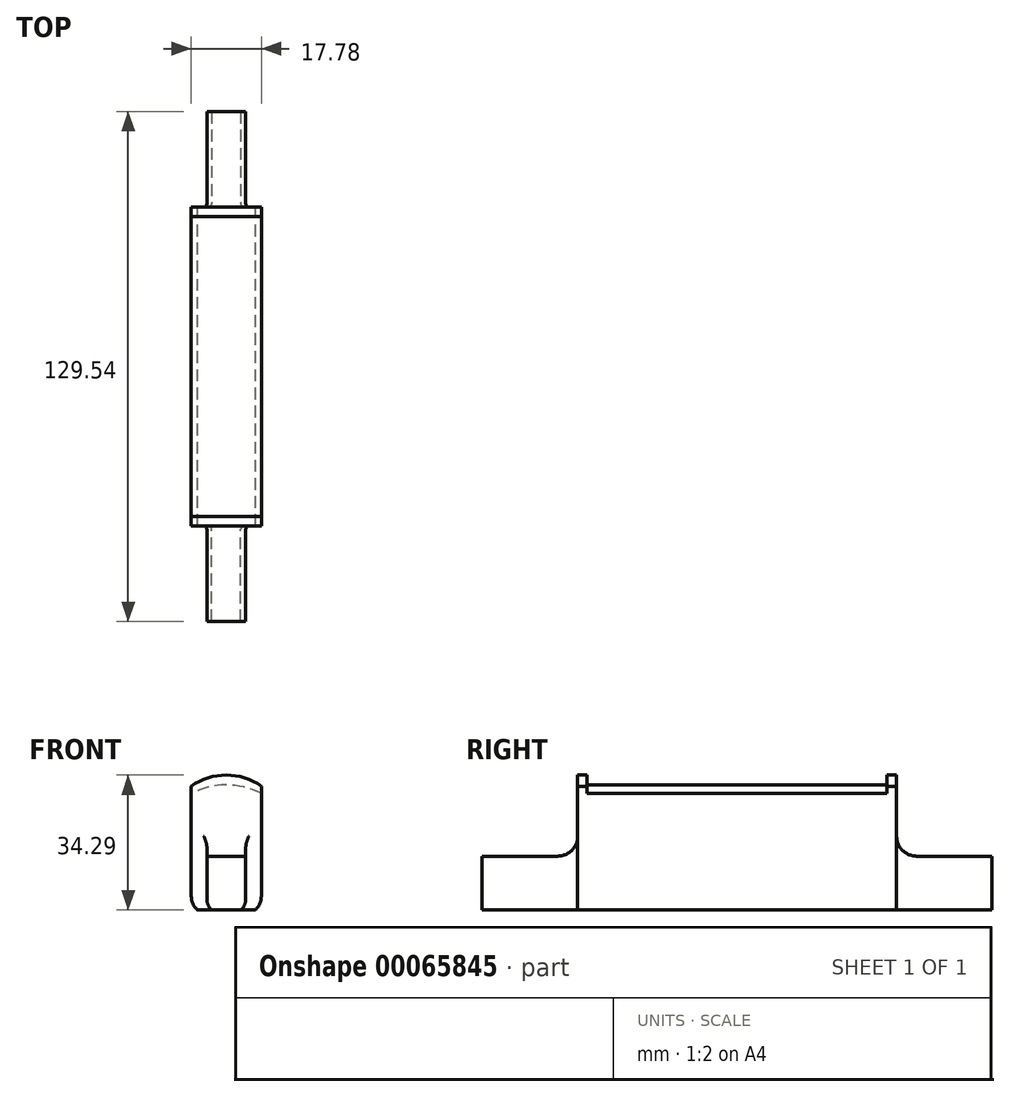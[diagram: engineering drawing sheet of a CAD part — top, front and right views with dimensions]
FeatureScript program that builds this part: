
annotation { "Feature Type Name" : "Feature", "Feature Type Description" : "" }
export const myFeature = defineFeature(function(context is Context, id is Id, definition is map)
    precondition{}
    {
        {
            var Q0;
            Q0=qCreatedBy(makeId("Front.planeOp"),FACE);
            var sketch = newSketch(context, id + "F0", { "sketchPlane" : qUnion([Q0])});
            skLineSegment(sketch, "E0.rect.bottom", {"start": v(8.9, 24.58) * mm, "end": v(-8.9, 24.58) * mm});
            skLineSegment(sketch, "E0.rect.top", {"start": v(8.89, -6.83) * mm, "end": v(-8.9, -6.83) * mm});
            skLineSegment(sketch, "E0.rect.left", {"start": v(8.89, 24.58) * mm, "end": v(8.89, -6.83) * mm});
            skLineSegment(sketch, "E0.rect.right", {"start": v(-8.9, 24.58) * mm, "end": v(-8.9, -6.83) * mm});
            skPoint(sketch, "E0.rect.middle", {"position": v(0, 8.87) * mm});
            skCircle(sketch, "E1", {"center": v(0, 0) * mm, "radius": 4.95 * mm});
            skArc(sketch, "E2", {"start": v(8.89, 24.58) * mm, "mid": v(0, 27.46) * mm, "end": v(-8.9, 24.58) * mm});
            skLineSegment(sketch, "E3.rect.bottom", {"start": v(-4.95, 6.83) * mm, "end": v(4.95, 6.83) * mm});
            skLineSegment(sketch, "E3.rect.top", {"start": v(-4.95, -6.83) * mm, "end": v(4.95, -6.83) * mm});
            skLineSegment(sketch, "E3.rect.left", {"start": v(-4.95, 6.83) * mm, "end": v(-4.95, -6.83) * mm});
            skLineSegment(sketch, "E3.rect.right", {"start": v(4.95, 6.83) * mm, "end": v(4.95, -6.83) * mm});
            skLineSegment(sketch, "E4", {"start": v(-8.89, 22.73) * mm, "end": v(8.9, 22.73) * mm});
            skArc(sketch, "E5", {"start": v(8.89, 22.73) * mm, "mid": v(0, 24.92) * mm, "end": v(-8.9, 22.73) * mm});
            skLineSegment(sketch, "E6", {"start": v(0, 27.46) * mm, "end": v(0, 24.92) * mm, "construction": true});
            skArc(sketch, "E7", {"start": v(-8.89, -3.43) * mm, "mid": v(-8.5, -5.3) * mm, "end": v(-7.37, -6.83) * mm});
            skArc(sketch, "E8", {"start": v(7.37, -6.83) * mm, "mid": v(8.5, -5.3) * mm, "end": v(8.9, -3.43) * mm});
            skArc(sketch, "E9", {"start": v(-4.95, -4.1) * mm, "mid": v(-4.62, -5.61) * mm, "end": v(-3.68, -6.83) * mm});
            skArc(sketch, "E10", {"start": v(3.68, -6.83) * mm, "mid": v(4.62, -5.61) * mm, "end": v(4.95, -4.1) * mm});
            skCircle(sketch, "E11", {"center": v(0, -4.3) * mm, "radius": 29.21 * mm, "construction": true});
            skCircle(sketch, "E12", {"center": v(0, 5.87) * mm, "radius": 19.05 * mm, "construction": true});
            skSolve(sketch);
        }
        {
            var Q0;
            {var subQ0=sQuery(id+"F0.wireOp",EDGE,"E5");var subQ1=sQuery(id+"F0.wireOp",EDGE,"E0.rect.bottom");var subQ2=makeQuery(id+"F0.imprint","INTERSECT",VERTEX,{"disambiguationData":[OD(0.0)],"derivedFrom":[subQ1,subQ0]});Q0=makeQuery(id+"F0.imprint","IMPRINT",FACE,{"disambiguationData":[TD([[makeQuery(id+"F0.imprint","IMPRINT",EDGE,{"disambiguationData":[TD([[subQ2,1.0]])],"derivedFrom":subQ1}),1.0]])]});}
            var Q1;
            {var subQ0=sQuery(id+"F0.wireOp",EDGE,"E5");var subQ1=sQuery(id+"F0.wireOp",EDGE,"E0.rect.bottom");var subQ2=makeQuery(id+"F0.imprint","INTERSECT",VERTEX,{"disambiguationData":[OD(1.0)],"derivedFrom":[subQ1,subQ0]});Q1=makeQuery(id+"F0.imprint","IMPRINT",FACE,{"disambiguationData":[TD([[makeQuery(id+"F0.imprint","IMPRINT",EDGE,{"disambiguationData":[TD([[subQ2,-1.0]])],"derivedFrom":subQ1}),1.0]])]});}
            var Q2;
            {var subQ1=sQuery(id+"F0.wireOp",EDGE,"E9");Q2=makeQuery(id+"F0.imprint","IMPRINT",FACE,{"disambiguationData":[TD([[makeQuery(id+"F0.imprint","IMPRINT",EDGE,{"derivedFrom":subQ1}),-1.0]])]});}
            var Q3;
            {var subQ0=sQuery(id+"F0.wireOp",EDGE,"E10");Q3=makeQuery(id+"F0.imprint","IMPRINT",FACE,{"disambiguationData":[TD([[makeQuery(id+"F0.imprint","IMPRINT",EDGE,{"derivedFrom":subQ0}),-1.0]])]});}
            var Q4;
            {var subQ4=sQuery(id+"F0.wireOp",EDGE,"E2");Q4=makeQuery(id+"F0.imprint","IMPRINT",FACE,{"disambiguationData":[TD([[makeQuery(id+"F0.imprint","IMPRINT",EDGE,{"derivedFrom":subQ4}),1.0]])]});}
            var Q5;
            {var subQ3=sQuery(id+"F0.wireOp",EDGE,"E4");Q5=makeQuery(id+"F0.imprint","IMPRINT",FACE,{"disambiguationData":[TD([[makeQuery(id+"F0.imprint","IMPRINT",EDGE,{"derivedFrom":subQ3}),1.0]])]});}
            var Q6;
            {var subQ7=sQuery(id+"F0.wireOp",EDGE,"E9");Q6=makeQuery(id+"F0.imprint","IMPRINT",FACE,{"disambiguationData":[TD([[makeQuery(id+"F0.imprint","IMPRINT",EDGE,{"derivedFrom":subQ7}),1.0]])]});}
            var Q7;
            {var subQ12=sQuery(id+"F0.wireOp",EDGE,"E3.rect.bottom");Q7=makeQuery(id+"F0.imprint","IMPRINT",FACE,{"disambiguationData":[TD([[makeQuery(id+"F0.imprint","IMPRINT",EDGE,{"derivedFrom":subQ12}),1.0]])]});}
            var Q8;
            {var subQ0=sQuery(id+"F0.wireOp",EDGE,"E5");var subQ1=sQuery(id+"F0.wireOp",EDGE,"E0.rect.bottom");var subQ3=makeQuery(id+"F0.imprint","INTERSECT",VERTEX,{"disambiguationData":[OD(0.0)],"derivedFrom":[subQ1,subQ0]});Q8=makeQuery(id+"F0.imprint","IMPRINT",FACE,{"disambiguationData":[TD([[makeQuery(id+"F0.imprint","IMPRINT",EDGE,{"disambiguationData":[TD([[subQ3,-1.0]])],"derivedFrom":subQ1}),-1.0]])]});}
            var Q9;
            {var subQ3=sQuery(id+"F0.wireOp",EDGE,"E3.rect.bottom");Q9=makeQuery(id+"F0.imprint","IMPRINT",FACE,{"disambiguationData":[TD([[makeQuery(id+"F0.imprint","IMPRINT",EDGE,{"derivedFrom":subQ3}),-1.0]])]});}
            var Q10;
            {var subQ0=sQuery(id+"F0.wireOp",EDGE,"E1");var subQ2=makeQuery(id+"F0.imprint","INTERSECT",VERTEX,{"derivedFrom":[subQ0,sQuery(id+"F0.wireOp",EDGE,"E3.rect.left")]});Q10=makeQuery(id+"F0.imprint","IMPRINT",FACE,{"disambiguationData":[TD([[makeQuery(id+"F0.imprint","IMPRINT",EDGE,{"disambiguationData":[TD([[subQ2,1.0]])],"derivedFrom":subQ0}),1.0]])]});}
            extrude(context, id + "F1", {"entities" : qUnion([Q0, Q1, Q2, Q3, Q4, Q5, Q6, Q7, Q8, Q9, Q10]), "depth" : 40.5 * mm});
        }
        {
            var Q0;
            {var subQ0=sQuery(id+"F0.wireOp",EDGE,"E5");var subQ1=sQuery(id+"F0.wireOp",EDGE,"E0.rect.bottom");var subQ2=makeQuery(id+"F0.imprint","INTERSECT",VERTEX,{"disambiguationData":[OD(1.0)],"derivedFrom":[subQ1,subQ0]});Q0=makeQuery(id+"F0.imprint","IMPRINT",FACE,{"disambiguationData":[TD([[makeQuery(id+"F0.imprint","IMPRINT",EDGE,{"disambiguationData":[TD([[subQ2,-1.0]])],"derivedFrom":subQ1}),1.0]])]});}
            var Q1;
            {var subQ4=sQuery(id+"F0.wireOp",EDGE,"E2");Q1=makeQuery(id+"F0.imprint","IMPRINT",FACE,{"disambiguationData":[TD([[makeQuery(id+"F0.imprint","IMPRINT",EDGE,{"derivedFrom":subQ4}),1.0]])]});}
            var Q2;
            {var subQ0=sQuery(id+"F0.wireOp",EDGE,"E5");var subQ1=sQuery(id+"F0.wireOp",EDGE,"E0.rect.bottom");var subQ2=makeQuery(id+"F0.imprint","INTERSECT",VERTEX,{"disambiguationData":[OD(0.0)],"derivedFrom":[subQ1,subQ0]});Q2=makeQuery(id+"F0.imprint","IMPRINT",FACE,{"disambiguationData":[TD([[makeQuery(id+"F0.imprint","IMPRINT",EDGE,{"disambiguationData":[TD([[subQ2,1.0]])],"derivedFrom":subQ1}),1.0]])]});}
            extrude(context, id + "F2", {"entities" : qUnion([Q0, Q1, Q2]), "operationType" : NewBodyOperationType.REMOVE, "depth" : 38.1 * mm});
        }
        {
            var Q0;
            {var subQ7=sQuery(id+"F0.wireOp",EDGE,"E9");Q0=makeQuery(id+"F0.imprint","IMPRINT",FACE,{"disambiguationData":[TD([[makeQuery(id+"F0.imprint","IMPRINT",EDGE,{"derivedFrom":subQ7}),1.0]])]});}
            var Q1;
            {var subQ0=sQuery(id+"F0.wireOp",EDGE,"E1");var subQ2=makeQuery(id+"F0.imprint","INTERSECT",VERTEX,{"derivedFrom":[subQ0,sQuery(id+"F0.wireOp",EDGE,"E3.rect.left")]});Q1=makeQuery(id+"F0.imprint","IMPRINT",FACE,{"disambiguationData":[TD([[makeQuery(id+"F0.imprint","IMPRINT",EDGE,{"disambiguationData":[TD([[subQ2,1.0]])],"derivedFrom":subQ0}),1.0]])]});}
            var Q2;
            {var subQ3=sQuery(id+"F0.wireOp",EDGE,"E3.rect.bottom");Q2=makeQuery(id+"F0.imprint","IMPRINT",FACE,{"disambiguationData":[TD([[makeQuery(id+"F0.imprint","IMPRINT",EDGE,{"derivedFrom":subQ3}),-1.0]])]});}
            extrude(context, id + "F3", {"entities" : qUnion([Q0, Q1, Q2]), "operationType" : NewBodyOperationType.ADD, "depth" : 64.77 * mm});
        }
        {
            var Q0;
            Q0=makeQuery(id+"F1.opExtrude","SWEPT_BODY",BODY,{"disambiguationData":[OSD([sQuery(id+"F0.wireOp",EDGE,"E0.rect.top"),sQuery(id+"F0.wireOp",EDGE,"E0.rect.left"),sQuery(id+"F0.wireOp",EDGE,"E0.rect.right"),sQuery(id+"F0.wireOp",EDGE,"E2"),sQuery(id+"F0.wireOp",EDGE,"E3.rect.top"),sQuery(id+"F0.wireOp",EDGE,"E7"),sQuery(id+"F0.wireOp",EDGE,"E8")])]});
            var Q1;
            Q1=qCreatedBy(makeId("Front.planeOp"),FACE);
            mirror(context, id + "F4", {"operationType" : NewBodyOperationType.ADD, "entities" : qUnion([Q0]), "mirrorPlane" : qUnion([Q1])});
        }
        {
            var Q0;
            Q0=makeQuery(id+"F3.boolean.opBoolean","INTERSECT",EDGE,{"derivedFrom":[makeQuery(id+"F1.opExtrude","CAP_FACE",FACE,{"disambiguationData":[OSD([sQuery(id+"F0.wireOp",EDGE,"E0.rect.top"),sQuery(id+"F0.wireOp",EDGE,"E0.rect.left"),sQuery(id+"F0.wireOp",EDGE,"E0.rect.right"),sQuery(id+"F0.wireOp",EDGE,"E2"),sQuery(id+"F0.wireOp",EDGE,"E3.rect.top"),sQuery(id+"F0.wireOp",EDGE,"E7"),sQuery(id+"F0.wireOp",EDGE,"E8")])],"isStart":false}),makeQuery(id+"F3.opExtrude","SWEPT_FACE",FACE,{"disambiguationData":[OSD([sQuery(id+"F0.wireOp",EDGE,"E3.rect.bottom")])]})]});
            var Q1;
            Q1=makeQuery(id+"F4.opPattern","COPY",EDGE,{"derivedFrom":makeQuery(id+"F3.boolean.opBoolean","INTERSECT",EDGE,{"derivedFrom":[makeQuery(id+"F1.opExtrude","CAP_FACE",FACE,{"disambiguationData":[OSD([sQuery(id+"F0.wireOp",EDGE,"E0.rect.top"),sQuery(id+"F0.wireOp",EDGE,"E0.rect.left"),sQuery(id+"F0.wireOp",EDGE,"E0.rect.right"),sQuery(id+"F0.wireOp",EDGE,"E2"),sQuery(id+"F0.wireOp",EDGE,"E3.rect.top"),sQuery(id+"F0.wireOp",EDGE,"E7"),sQuery(id+"F0.wireOp",EDGE,"E8")])],"isStart":false}),makeQuery(id+"F3.opExtrude","SWEPT_FACE",FACE,{"disambiguationData":[OSD([sQuery(id+"F0.wireOp",EDGE,"E3.rect.bottom")])]})]}),"instanceName":"1"});
            fillet(context, id + "F5", {"entities" : qUnion([Q0, Q1]), "radius" : 5.08 * mm, "tangentPropagation" : true, "allowEdgeOverflow" : false});
        }
        {
            var Q0;
            Q0=makeQuery(id+"F4.opPattern","COPY",EDGE,{"derivedFrom":makeQuery(id+"F3.boolean.opBoolean","INTERSECT",EDGE,{"derivedFrom":[makeQuery(id+"F1.opExtrude","CAP_FACE",FACE,{"disambiguationData":[OSD([sQuery(id+"F0.wireOp",EDGE,"E0.rect.top"),sQuery(id+"F0.wireOp",EDGE,"E0.rect.left"),sQuery(id+"F0.wireOp",EDGE,"E0.rect.right"),sQuery(id+"F0.wireOp",EDGE,"E2"),sQuery(id+"F0.wireOp",EDGE,"E3.rect.top"),sQuery(id+"F0.wireOp",EDGE,"E7"),sQuery(id+"F0.wireOp",EDGE,"E8")])],"isStart":false}),makeQuery(id+"F3.opExtrude","SWEPT_FACE",FACE,{"disambiguationData":[OSD([sQuery(id+"F0.wireOp",EDGE,"E3.rect.left")])]})]}),"instanceName":"1"});
            var Q1;
            Q1=makeQuery(id+"F4.opPattern","COPY",EDGE,{"derivedFrom":makeQuery(id+"F3.boolean.opBoolean","INTERSECT",EDGE,{"derivedFrom":[makeQuery(id+"F1.opExtrude","CAP_FACE",FACE,{"disambiguationData":[OSD([sQuery(id+"F0.wireOp",EDGE,"E0.rect.top"),sQuery(id+"F0.wireOp",EDGE,"E0.rect.left"),sQuery(id+"F0.wireOp",EDGE,"E0.rect.right"),sQuery(id+"F0.wireOp",EDGE,"E2"),sQuery(id+"F0.wireOp",EDGE,"E3.rect.top"),sQuery(id+"F0.wireOp",EDGE,"E7"),sQuery(id+"F0.wireOp",EDGE,"E8")])],"isStart":false}),makeQuery(id+"F3.opExtrude","SWEPT_FACE",FACE,{"disambiguationData":[OSD([sQuery(id+"F0.wireOp",EDGE,"E9")])]})]}),"instanceName":"1"});
            var Q2;
            Q2=makeQuery(id+"F3.boolean.opBoolean","INTERSECT",EDGE,{"derivedFrom":[makeQuery(id+"F1.opExtrude","CAP_FACE",FACE,{"disambiguationData":[OSD([sQuery(id+"F0.wireOp",EDGE,"E0.rect.top"),sQuery(id+"F0.wireOp",EDGE,"E0.rect.left"),sQuery(id+"F0.wireOp",EDGE,"E0.rect.right"),sQuery(id+"F0.wireOp",EDGE,"E2"),sQuery(id+"F0.wireOp",EDGE,"E3.rect.top"),sQuery(id+"F0.wireOp",EDGE,"E7"),sQuery(id+"F0.wireOp",EDGE,"E8")])],"isStart":false}),makeQuery(id+"F3.opExtrude","SWEPT_FACE",FACE,{"disambiguationData":[OSD([sQuery(id+"F0.wireOp",EDGE,"E3.rect.left")])]})]});
            var Q3;
            Q3=makeQuery(id+"F3.boolean.opBoolean","INTERSECT",EDGE,{"derivedFrom":[makeQuery(id+"F1.opExtrude","CAP_FACE",FACE,{"disambiguationData":[OSD([sQuery(id+"F0.wireOp",EDGE,"E0.rect.top"),sQuery(id+"F0.wireOp",EDGE,"E0.rect.left"),sQuery(id+"F0.wireOp",EDGE,"E0.rect.right"),sQuery(id+"F0.wireOp",EDGE,"E2"),sQuery(id+"F0.wireOp",EDGE,"E3.rect.top"),sQuery(id+"F0.wireOp",EDGE,"E7"),sQuery(id+"F0.wireOp",EDGE,"E8")])],"isStart":false}),makeQuery(id+"F3.opExtrude","SWEPT_FACE",FACE,{"disambiguationData":[OSD([sQuery(id+"F0.wireOp",EDGE,"E9")])]})]});
            var Q4;
            Q4=makeQuery(id+"F3.boolean.opBoolean","INTERSECT",EDGE,{"derivedFrom":[makeQuery(id+"F1.opExtrude","CAP_FACE",FACE,{"disambiguationData":[OSD([sQuery(id+"F0.wireOp",EDGE,"E0.rect.top"),sQuery(id+"F0.wireOp",EDGE,"E0.rect.left"),sQuery(id+"F0.wireOp",EDGE,"E0.rect.right"),sQuery(id+"F0.wireOp",EDGE,"E2"),sQuery(id+"F0.wireOp",EDGE,"E3.rect.top"),sQuery(id+"F0.wireOp",EDGE,"E7"),sQuery(id+"F0.wireOp",EDGE,"E8")])],"isStart":false}),makeQuery(id+"F3.opExtrude","SWEPT_FACE",FACE,{"disambiguationData":[OSD([sQuery(id+"F0.wireOp",EDGE,"E10")])]})]});
            var Q5;
            Q5=makeQuery(id+"F3.boolean.opBoolean","INTERSECT",EDGE,{"derivedFrom":[makeQuery(id+"F1.opExtrude","CAP_FACE",FACE,{"disambiguationData":[OSD([sQuery(id+"F0.wireOp",EDGE,"E0.rect.top"),sQuery(id+"F0.wireOp",EDGE,"E0.rect.left"),sQuery(id+"F0.wireOp",EDGE,"E0.rect.right"),sQuery(id+"F0.wireOp",EDGE,"E2"),sQuery(id+"F0.wireOp",EDGE,"E3.rect.top"),sQuery(id+"F0.wireOp",EDGE,"E7"),sQuery(id+"F0.wireOp",EDGE,"E8")])],"isStart":false}),makeQuery(id+"F3.opExtrude","SWEPT_FACE",FACE,{"disambiguationData":[OSD([sQuery(id+"F0.wireOp",EDGE,"E3.rect.right")])]})]});
            var Q6;
            Q6=makeQuery(id+"F4.opPattern","COPY",EDGE,{"derivedFrom":makeQuery(id+"F3.boolean.opBoolean","INTERSECT",EDGE,{"derivedFrom":[makeQuery(id+"F1.opExtrude","CAP_FACE",FACE,{"disambiguationData":[OSD([sQuery(id+"F0.wireOp",EDGE,"E0.rect.top"),sQuery(id+"F0.wireOp",EDGE,"E0.rect.left"),sQuery(id+"F0.wireOp",EDGE,"E0.rect.right"),sQuery(id+"F0.wireOp",EDGE,"E2"),sQuery(id+"F0.wireOp",EDGE,"E3.rect.top"),sQuery(id+"F0.wireOp",EDGE,"E7"),sQuery(id+"F0.wireOp",EDGE,"E8")])],"isStart":false}),makeQuery(id+"F3.opExtrude","SWEPT_FACE",FACE,{"disambiguationData":[OSD([sQuery(id+"F0.wireOp",EDGE,"E3.rect.right")])]})]}),"instanceName":"1"});
            var Q7;
            Q7=makeQuery(id+"F4.opPattern","COPY",EDGE,{"derivedFrom":makeQuery(id+"F3.boolean.opBoolean","INTERSECT",EDGE,{"derivedFrom":[makeQuery(id+"F1.opExtrude","CAP_FACE",FACE,{"disambiguationData":[OSD([sQuery(id+"F0.wireOp",EDGE,"E0.rect.top"),sQuery(id+"F0.wireOp",EDGE,"E0.rect.left"),sQuery(id+"F0.wireOp",EDGE,"E0.rect.right"),sQuery(id+"F0.wireOp",EDGE,"E2"),sQuery(id+"F0.wireOp",EDGE,"E3.rect.top"),sQuery(id+"F0.wireOp",EDGE,"E7"),sQuery(id+"F0.wireOp",EDGE,"E8")])],"isStart":false}),makeQuery(id+"F3.opExtrude","SWEPT_FACE",FACE,{"disambiguationData":[OSD([sQuery(id+"F0.wireOp",EDGE,"E10")])]})]}),"instanceName":"1"});
            fillet(context, id + "F6", {"entities" : qUnion([Q0, Q1, Q2, Q3, Q4, Q5, Q6, Q7]), "radius" : 0.76 * mm, "tangentPropagation" : true, "allowEdgeOverflow" : false});
        }
    });
